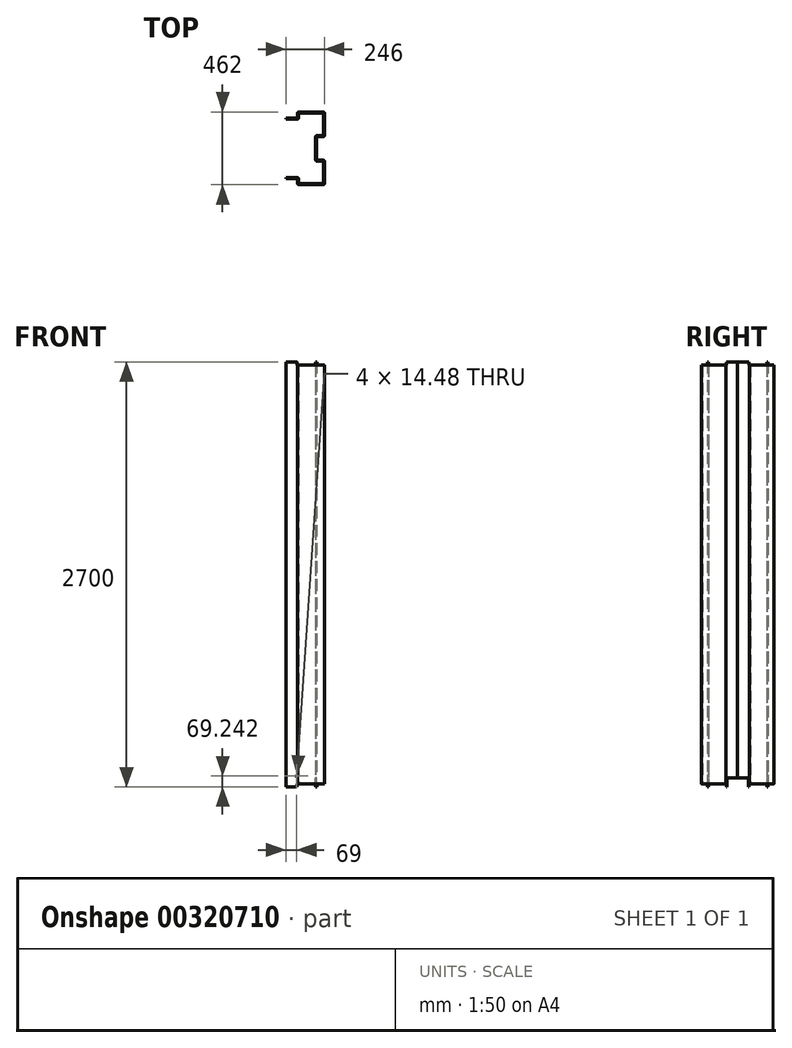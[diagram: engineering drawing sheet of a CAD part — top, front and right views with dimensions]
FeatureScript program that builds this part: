
annotation { "Feature Type Name" : "Feature", "Feature Type Description" : "" }
export const myFeature = defineFeature(function(context is Context, id is Id, definition is map)
    precondition{}
    {
        {
            var Q0;
            Q0=qCreatedBy(makeId("Top.planeOp"),FACE);
            var sketch = newSketch(context, id + "F0", { "sketchPlane" : qUnion([Q0])});
            skLineSegment(sketch, "E0", {"start": v(-44.59, 0) * mm, "end": v(-44.59, 6) * mm});
            skLineSegment(sketch, "E1", {"start": v(-44.59, 6) * mm, "end": v(28.41, 6) * mm});
            skLineSegment(sketch, "E2", {"start": v(-44.59, 0) * mm, "end": v(22.41, 0) * mm});
            skLineSegment(sketch, "E3", {"start": v(36.41, -2) * mm, "end": v(36.41, -25) * mm});
            skLineSegment(sketch, "E4", {"start": v(30.41, -8) * mm, "end": v(30.41, -31) * mm});
            skLineSegment(sketch, "E5", {"start": v(38.41, -39) * mm, "end": v(193.41, -39) * mm});
            skLineSegment(sketch, "E6", {"start": v(44.41, -33) * mm, "end": v(187.41, -33) * mm});
            skLineSegment(sketch, "E7", {"start": v(201.41, -31) * mm, "end": v(201.41, 109) * mm});
            skLineSegment(sketch, "E8", {"start": v(195.41, -25) * mm, "end": v(195.41, 103) * mm});
            skLineSegment(sketch, "E9", {"start": v(193.41, 117) * mm, "end": v(159.41, 117) * mm});
            skLineSegment(sketch, "E10", {"start": v(187.41, 111) * mm, "end": v(153.41, 111) * mm});
            skLineSegment(sketch, "E11", {"start": v(151.41, 125) * mm, "end": v(151.41, 192) * mm});
            skLineSegment(sketch, "E12", {"start": v(151.41, 192) * mm, "end": v(145.41, 192) * mm});
            skLineSegment(sketch, "E13", {"start": v(145.41, 192) * mm, "end": v(145.41, 119) * mm});
            skPoint(sketch, "E14.visualSharp", {"position": v(151.41, 117) * mm});
            skArc(sketch, "E14.filletArc", {"start": v(151.41, 125) * mm, "mid": v(153.75, 119.34) * mm, "end": v(159.41, 117) * mm});
            skPoint(sketch, "E15.visualSharp", {"position": v(145.41, 111) * mm});
            skArc(sketch, "E15.filletArc", {"start": v(145.41, 119) * mm, "mid": v(147.75, 113.34) * mm, "end": v(153.41, 111) * mm});
            skPoint(sketch, "E16.visualSharp", {"position": v(195.41, 111) * mm});
            skArc(sketch, "E16.filletArc", {"start": v(195.41, 103) * mm, "mid": v(193.07, 108.66) * mm, "end": v(187.41, 111) * mm});
            skPoint(sketch, "E17.visualSharp", {"position": v(195.41, -33) * mm});
            skArc(sketch, "E17.filletArc", {"start": v(187.41, -33) * mm, "mid": v(193.07, -30.66) * mm, "end": v(195.41, -25) * mm});
            skPoint(sketch, "E18.visualSharp", {"position": v(201.41, 117) * mm});
            skArc(sketch, "E18.filletArc", {"start": v(201.41, 109) * mm, "mid": v(199.07, 114.66) * mm, "end": v(193.41, 117) * mm});
            skPoint(sketch, "E19.visualSharp", {"position": v(201.41, -39) * mm});
            skArc(sketch, "E19.filletArc", {"start": v(193.41, -39) * mm, "mid": v(199.07, -36.66) * mm, "end": v(201.41, -31) * mm});
            skPoint(sketch, "E20.visualSharp", {"position": v(30.41, -39) * mm});
            skArc(sketch, "E20.filletArc", {"start": v(30.41, -31) * mm, "mid": v(32.75, -36.66) * mm, "end": v(38.41, -39) * mm});
            skPoint(sketch, "E21.visualSharp", {"position": v(36.41, -33) * mm});
            skArc(sketch, "E21.filletArc", {"start": v(36.41, -25) * mm, "mid": v(38.75, -30.66) * mm, "end": v(44.41, -33) * mm});
            skPoint(sketch, "E22.visualSharp", {"position": v(36.41, 6) * mm});
            skArc(sketch, "E22.filletArc", {"start": v(36.41, -2) * mm, "mid": v(34.07, 3.66) * mm, "end": v(28.41, 6) * mm});
            skPoint(sketch, "E23.visualSharp", {"position": v(30.41, 0) * mm});
            skArc(sketch, "E23.filletArc", {"start": v(30.41, -8) * mm, "mid": v(28.07, -2.34) * mm, "end": v(22.41, 0) * mm});
            skSolve(sketch);
        }
        {
            var Q0;
            Q0=qSketchRegion(id+"F0",true);
            extrude(context, id + "F1", {"entities" : qUnion([Q0]), "depth" : 2700 * mm});
        }
        {
            var Q0;
            Q0=makeQuery(id+"F1.opExtrude","SWEPT_FACE",FACE,{"disambiguationData":[OSD([sQuery(id+"F0.wireOp",EDGE,"E5")])]});
            var sketch = newSketch(context, id + "F2", { "sketchPlane" : qUnion([Q0])});
            skLineSegment(sketch, "E24.0", {"start": v(38.41, 2700) * mm, "end": v(193.41, 2700) * mm});
            skLineSegment(sketch, "E25.0", {"start": v(38.41, 0) * mm, "end": v(193.41, 0) * mm});
            skLineSegment(sketch, "E26", {"start": v(193.41, 1350) * mm, "end": v(193.41, 2680) * mm});
            skLineSegment(sketch, "E27.0", {"start": v(201.41, 2700) * mm, "end": v(201.41, 0) * mm});
            skLineSegment(sketch, "E28", {"start": v(201.41, 2700) * mm, "end": v(26.41, 2700) * mm});
            skLineSegment(sketch, "E29", {"start": v(26.41, 2700) * mm, "end": v(26.41, 2680) * mm});
            skLineSegment(sketch, "E30", {"start": v(26.41, 2680) * mm, "end": v(193.41, 2680) * mm});
            skLineSegment(sketch, "E31", {"start": v(193.41, 1350) * mm, "end": v(93.35, 1350) * mm});
            skLineSegment(sketch, "E32.MirrorCS", {"start": v(26.41, 20) * mm, "end": v(193.41, 20) * mm});
            skLineSegment(sketch, "E33.MirrorCS", {"start": v(26.41, 0) * mm, "end": v(26.41, 20) * mm});
            skLineSegment(sketch, "E34.MirrorCS", {"start": v(201.41, 0) * mm, "end": v(26.41, 0) * mm});
            skLineSegment(sketch, "E35", {"start": v(193.41, 20) * mm, "end": v(201.41, 20) * mm});
            skLineSegment(sketch, "E36", {"start": v(193.41, 2680) * mm, "end": v(201.41, 2680) * mm});
            skSolve(sketch);
        }
        {
            var Q0;
            Q0=qSketchRegion(id+"F2",true);
            extrude(context, id + "F3", {"entities" : qUnion([Q0]), "operationType" : NewBodyOperationType.REMOVE, "oppositeDirection" : true, "depth" : 159 * mm});
        }
        {
            var Q0;
            Q0=makeQuery(id+"F1.opExtrude","SWEPT_FACE",FACE,{"disambiguationData":[OSD([sQuery(id+"F0.wireOp",EDGE,"E13")])]});
            var sketch = newSketch(context, id + "F4", { "sketchPlane" : qUnion([Q0])});
            skLineSegment(sketch, "E37.bottom", {"start": v(-192, 0) * mm, "end": v(-125, 0) * mm});
            skLineSegment(sketch, "E37.top", {"start": v(-192, 56.32) * mm, "end": v(-125, 56.32) * mm});
            skLineSegment(sketch, "E37.left", {"start": v(-192, 0) * mm, "end": v(-192, 56.32) * mm});
            skLineSegment(sketch, "E37.right", {"start": v(-125, 0) * mm, "end": v(-125, 56.32) * mm});
            skSolve(sketch);
        }
        {
            var Q0;
            Q0=makeQuery(id+"F4.imprint","IMPRINT",FACE,{"disambiguationData":[TD([[makeQuery(id+"F4.imprint","IMPRINT",EDGE,{"derivedFrom":sQuery(id+"F4.wireOp",EDGE,"E37.bottom")}),1.0]])]});
            extrude(context, id + "F5", {"entities" : qUnion([Q0]), "operationType" : NewBodyOperationType.REMOVE, "oppositeDirection" : true, "depth" : 25 * mm});
        }
        {
            var Q0;
            Q0=makeQuery(id+"F1.opExtrude","SWEPT_BODY",BODY,{"disambiguationData":[OSD([sQuery(id+"F0.wireOp",EDGE,"E0"),sQuery(id+"F0.wireOp",EDGE,"E1"),sQuery(id+"F0.wireOp",EDGE,"E2"),sQuery(id+"F0.wireOp",EDGE,"E3"),sQuery(id+"F0.wireOp",EDGE,"E4"),sQuery(id+"F0.wireOp",EDGE,"E5"),sQuery(id+"F0.wireOp",EDGE,"E6"),sQuery(id+"F0.wireOp",EDGE,"E7"),sQuery(id+"F0.wireOp",EDGE,"E8"),sQuery(id+"F0.wireOp",EDGE,"E9"),sQuery(id+"F0.wireOp",EDGE,"E10"),sQuery(id+"F0.wireOp",EDGE,"E11"),sQuery(id+"F0.wireOp",EDGE,"E12"),sQuery(id+"F0.wireOp",EDGE,"E13"),sQuery(id+"F0.wireOp",EDGE,"E14.filletArc"),sQuery(id+"F0.wireOp",EDGE,"E15.filletArc"),sQuery(id+"F0.wireOp",EDGE,"E16.filletArc"),sQuery(id+"F0.wireOp",EDGE,"E17.filletArc"),sQuery(id+"F0.wireOp",EDGE,"E18.filletArc"),sQuery(id+"F0.wireOp",EDGE,"E19.filletArc"),sQuery(id+"F0.wireOp",EDGE,"E20.filletArc"),sQuery(id+"F0.wireOp",EDGE,"E21.filletArc"),sQuery(id+"F0.wireOp",EDGE,"E22.filletArc"),sQuery(id+"F0.wireOp",EDGE,"E23.filletArc")])]});
            var Q1;
            Q1=makeQuery(id+"F1.opExtrude","SWEPT_FACE",FACE,{"disambiguationData":[OSD([sQuery(id+"F0.wireOp",EDGE,"E12")])]});
            mirror(context, id + "F6", {"entities" : qUnion([Q0]), "mirrorPlane" : qUnion([Q1])});
        }
        {
            var Q0;
            Q0=makeQuery(id+"F6.opPattern","COPY",FACE,{"derivedFrom":makeQuery(id+"F1.opExtrude","SWEPT_FACE",FACE,{"disambiguationData":[OSD([sQuery(id+"F0.wireOp",EDGE,"E2")])]}),"instanceName":"1"});
            var sketch = newSketch(context, id + "F7", { "sketchPlane" : qUnion([Q0])});
            skLineSegment(sketch, "E38.0", {"start": v(44.59, 2700) * mm, "end": v(44.59, 0) * mm});
            skLineSegment(sketch, "E39.0", {"start": v(-26.41, 0) * mm, "end": v(-26.41, 20) * mm});
            skLineSegment(sketch, "E40.bottom", {"start": v(44.59, 0) * mm, "end": v(-26.41, 0) * mm});
            skLineSegment(sketch, "E40.top", {"start": v(44.59, 62) * mm, "end": v(-26.41, 62) * mm});
            skLineSegment(sketch, "E40.left", {"start": v(44.59, 0) * mm, "end": v(44.59, 62) * mm});
            skLineSegment(sketch, "E40.right", {"start": v(-26.41, 0) * mm, "end": v(-26.41, 62) * mm});
            skLineSegment(sketch, "E41.top", {"start": v(44.59, 76.48) * mm, "end": v(-26.41, 76.48) * mm});
            skLineSegment(sketch, "E41.left", {"start": v(44.59, 0) * mm, "end": v(44.59, 76.48) * mm});
            skLineSegment(sketch, "E41.right", {"start": v(-26.41, 0) * mm, "end": v(-26.41, 76.48) * mm});
            skSolve(sketch);
        }
        {
            var Q0;
            {var subQ0=sQuery(id+"F7.wireOp",EDGE,"E41.right");var subQ1=sQuery(id+"F7.wireOp",EDGE,"E40.top");var subQ2=makeQuery(id+"F7.imprint","INTERSECT",VERTEX,{"derivedFrom":[subQ1,subQ0]});Q0=makeQuery(id+"F7.imprint","IMPRINT",FACE,{"disambiguationData":[TD([[makeQuery(id+"F7.imprint","IMPRINT",EDGE,{"disambiguationData":[TD([[subQ2,1.0]])],"derivedFrom":subQ0}),-1.0]])]});}
            var Q1;
            {var subQ0=sQuery(id+"F7.wireOp",EDGE,"E41.left");var subQ5=sQuery(id+"F7.wireOp",EDGE,"E40.bottom");var subQ6=makeQuery(id+"F7.imprint","INTERSECT",VERTEX,{"derivedFrom":[subQ5,subQ0]});Q1=makeQuery(id+"F7.imprint","IMPRINT",FACE,{"disambiguationData":[TD([[makeQuery(id+"F7.imprint","IMPRINT",EDGE,{"disambiguationData":[TD([[subQ6,1.0]])],"derivedFrom":subQ0}),-1.0]])]});}
            extrude(context, id + "F8", {"entities" : qUnion([Q0, Q1]), "operationType" : NewBodyOperationType.REMOVE, "endBound" : BoundingType.THROUGH_ALL, "oppositeDirection" : true, "depth" : 25 * mm, "hasSecondDirection" : true, "secondDirectionBound" : SecondDirectionBoundingType.THROUGH_ALL, "secondDirectionOppositeDirection" : false, "secondDirectionDepth" : 25 * mm});
        }
    });
